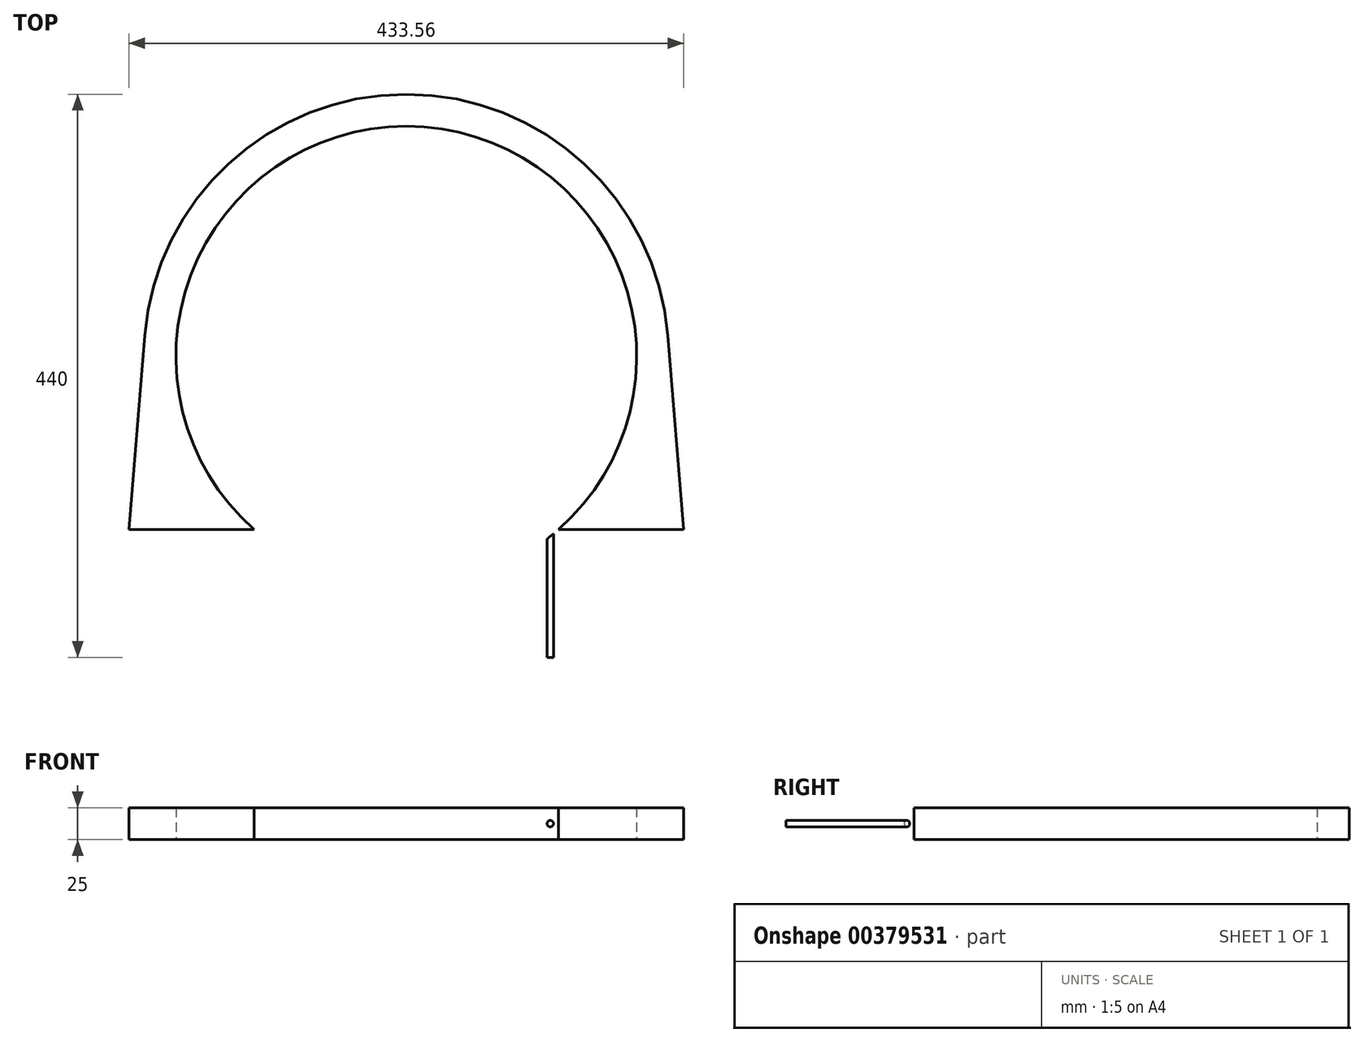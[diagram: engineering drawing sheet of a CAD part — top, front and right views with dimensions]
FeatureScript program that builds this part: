
annotation { "Feature Type Name" : "Feature", "Feature Type Description" : "" }
export const myFeature = defineFeature(function(context is Context, id is Id, definition is map)
    precondition{}
    {
        {
            var Q0;
            Q0=qCreatedBy(makeId("Top.planeOp"),FACE);
            var sketch = newSketch(context, id + "F0", { "sketchPlane" : qUnion([Q0])});
            skCircle(sketch, "E0", {"center": v(0, 0) * mm, "radius": 180 * mm});
            skCircle(sketch, "E1", {"center": v(0, 0) * mm, "radius": 205 * mm});
            skLineSegment(sketch, "E2", {"start": v(0, 0) * mm, "end": v(0, -423) * mm, "construction": true});
            skLineSegment(sketch, "E3", {"start": v(0, -235) * mm, "end": v(-225, -235) * mm});
            skLineSegment(sketch, "E4.MirrorCS", {"start": v(0, -235) * mm, "end": v(225, -235) * mm});
            skLineSegment(sketch, "E5", {"start": v(-225, -235) * mm, "end": v(-204.31, 16.79) * mm});
            skLineSegment(sketch, "E6.MirrorCS", {"start": v(225, -235) * mm, "end": v(204.31, 16.79) * mm});
            skSolve(sketch);
        }
        {
            var Q0;
            Q0=makeQuery(id+"F0.imprint","IMPRINT",FACE,{"disambiguationData":[TD([[makeQuery(id+"F0.imprint","IMPRINT",EDGE,{"derivedFrom":sQuery(id+"F0.wireOp",EDGE,"E3")}),-1.0]])]});
            var Q1;
            Q1=makeQuery(id+"F0.imprint","IMPRINT",FACE,{"disambiguationData":[TD([[makeQuery(id+"F0.imprint","IMPRINT",EDGE,{"derivedFrom":sQuery(id+"F0.wireOp",EDGE,"E0")}),-1.0]])]});
            extrude(context, id + "F1", {"entities" : qUnion([Q0, Q1]), "depth" : 25 * mm});
        }
        {
            var Q0;
            Q0=makeQuery(id+"F1.opExtrude","SWEPT_FACE",FACE,{"disambiguationData":[OSD([sQuery(id+"F0.wireOp",EDGE,"E3"),sQuery(id+"F0.wireOp",EDGE,"E4.MirrorCS")])]});
            var sketch = newSketch(context, id + "F2", { "sketchPlane" : qUnion([Q0])});
            skLineSegment(sketch, "E7", {"start": v(225, 0) * mm, "end": v(-225, 25) * mm, "construction": true});
            skLineSegment(sketch, "E8", {"start": v(-225, 25) * mm, "end": v(-225, 0) * mm, "construction": true});
            skLineSegment(sketch, "E9", {"start": v(-225, 0) * mm, "end": v(0, 25) * mm, "construction": true});
            skLineSegment(sketch, "E10", {"start": v(0, 25) * mm, "end": v(-225, 25) * mm, "construction": true});
            skLineSegment(sketch, "E11", {"start": v(225, 25) * mm, "end": v(-225, 0) * mm, "construction": true});
            skLineSegment(sketch, "E12", {"start": v(0, 0) * mm, "end": v(-225, 25) * mm, "construction": true});
            skCircle(sketch, "E13", {"center": v(0, 12.5) * mm, "radius": 2.5 * mm});
            skCircle(sketch, "E14", {"center": v(-112.5, 12.5) * mm, "radius": 2.5 * mm});
            skLineSegment(sketch, "E15", {"start": v(0, 12.5) * mm, "end": v(0, 25) * mm, "construction": true});
            skCircle(sketch, "E16.MirrorC", {"center": v(112.5, 12.5) * mm, "radius": 2.5 * mm});
            skSolve(sketch);
        }
        {
            var Q0;
            Q0=makeQuery(id+"F2.imprint","IMPRINT",FACE,{"disambiguationData":[TD([[makeQuery(id+"F2.imprint","IMPRINT",EDGE,{"derivedFrom":sQuery(id+"F2.wireOp",EDGE,"E16.MirrorC")}),-1.0]])]});
            var Q1;
            Q1=makeQuery(id+"F2.imprint","IMPRINT",FACE,{"disambiguationData":[TD([[makeQuery(id+"F2.imprint","IMPRINT",EDGE,{"derivedFrom":sQuery(id+"F2.wireOp",EDGE,"E13")}),1.0]])]});
            var Q2;
            Q2=makeQuery(id+"F2.imprint","IMPRINT",FACE,{"disambiguationData":[TD([[makeQuery(id+"F2.imprint","IMPRINT",EDGE,{"derivedFrom":sQuery(id+"F2.wireOp",EDGE,"E14")}),1.0]])]});
            extrude(context, id + "F3", {"entities" : qUnion([Q0, Q1, Q2]), "operationType" : NewBodyOperationType.REMOVE, "oppositeDirection" : true, "depth" : 100 * mm});
        }
    });
